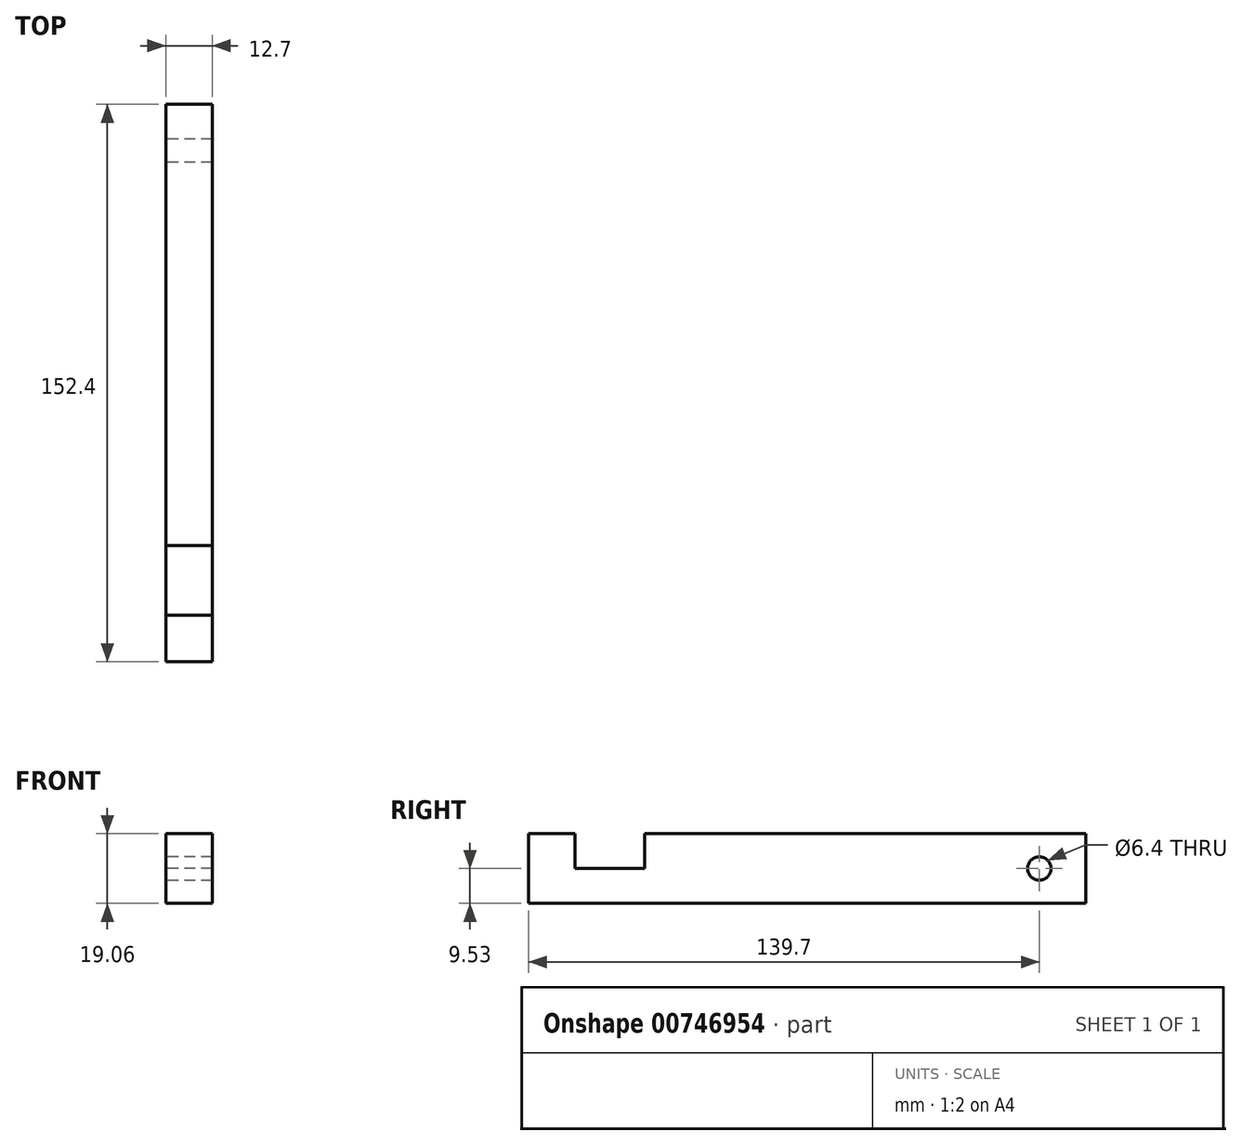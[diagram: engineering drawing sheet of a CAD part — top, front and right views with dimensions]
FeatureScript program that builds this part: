
annotation { "Feature Type Name" : "Feature", "Feature Type Description" : "" }
export const myFeature = defineFeature(function(context is Context, id is Id, definition is map)
    precondition{}
    {
        {
            var Q0;
            Q0=qCreatedBy(makeId("Right.planeOp"),FACE);
            var sketch = newSketch(context, id + "F0", { "sketchPlane" : qUnion([Q0])});
            skLineSegment(sketch, "E0.bottom", {"start": v(76.2, 9.53) * mm, "end": v(-44.45, 9.53) * mm});
            skLineSegment(sketch, "E0.top", {"start": v(76.2, -9.53) * mm, "end": v(-76.2, -9.53) * mm});
            skLineSegment(sketch, "E0.left", {"start": v(76.2, 9.53) * mm, "end": v(76.2, -9.53) * mm});
            skLineSegment(sketch, "E0.right", {"start": v(-76.2, 9.53) * mm, "end": v(-76.2, -9.53) * mm});
            skPoint(sketch, "E0.middle", {"position": v(0, 0) * mm});
            skCircle(sketch, "E1", {"center": v(63.5, 0) * mm, "radius": 3.2 * mm});
            skLineSegment(sketch, "E2.top", {"start": v(-63.5, 0) * mm, "end": v(-44.45, 0) * mm});
            skLineSegment(sketch, "E2.left", {"start": v(-63.5, 9.53) * mm, "end": v(-63.5, 0) * mm});
            skLineSegment(sketch, "E2.right", {"start": v(-44.45, 9.53) * mm, "end": v(-44.45, 0) * mm});
            skLineSegment(sketch, "E3.trimOffspring", {"start": v(-63.5, 9.53) * mm, "end": v(-76.2, 9.53) * mm});
            skSolve(sketch);
        }
        {
            var Q0;
            Q0=makeQuery(id+"F0.imprint","IMPRINT",FACE,{"disambiguationData":[TD([[makeQuery(id+"F0.imprint","IMPRINT",EDGE,{"derivedFrom":sQuery(id+"F0.wireOp",EDGE,"E0.top")}),-1.0]])]});
            extrude(context, id + "F1", {"entities" : qUnion([Q0]), "depth" : 12.7 * mm, "offsetDistance" : 25.4 * mm});
        }
    });
